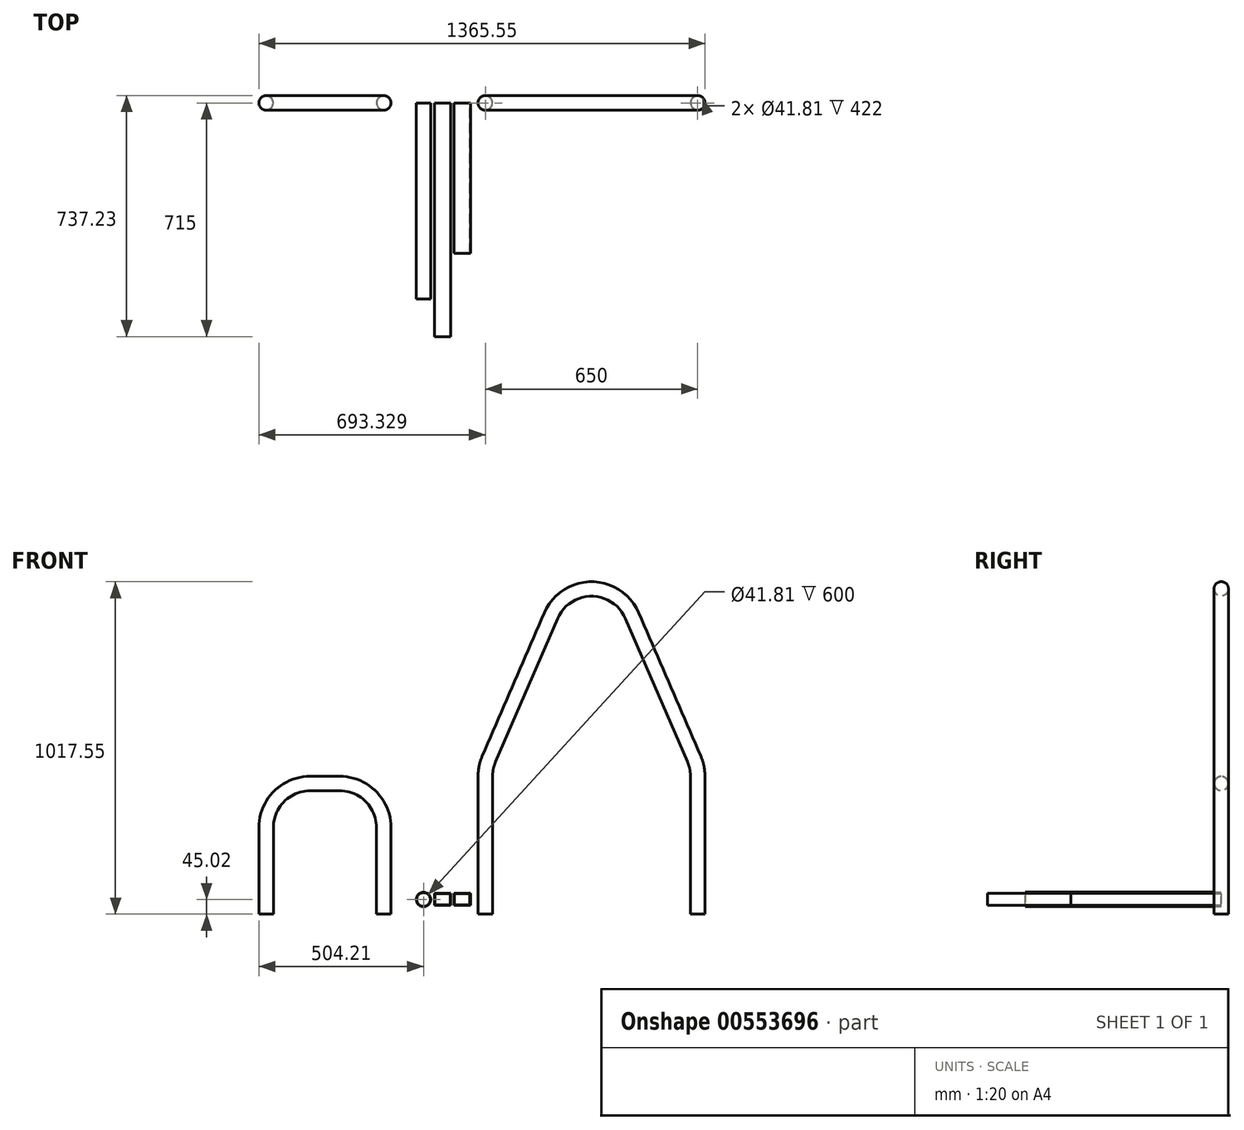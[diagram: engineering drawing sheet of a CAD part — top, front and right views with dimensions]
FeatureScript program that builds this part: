
annotation { "Feature Type Name" : "Feature", "Feature Type Description" : "" }
export const myFeature = defineFeature(function(context is Context, id is Id, definition is map)
    precondition{}
    {
        {
            var Q0;
            Q0=qCreatedBy(makeId("Front.planeOp"),FACE);
            var sketch = newSketch(context, id + "F0", { "sketchPlane" : qUnion([Q0])});
            skCircle(sketch, "E0", {"center": v(0, 0) * mm, "radius": 22.23 * mm});
            skCircle(sketch, "E1", {"center": v(0, 0) * mm, "radius": 20.9 * mm});
            skLineSegment(sketch, "E2.direction1", {"start": v(0, 0) * mm, "end": v(50, 0) * mm, "construction": true});
            skLineSegment(sketch, "E3.bottom", {"start": v(33.4, 18.7) * mm, "end": v(83.4, 18.7) * mm});
            skLineSegment(sketch, "E3.top", {"start": v(33.4, -18.35) * mm, "end": v(83.4, -18.35) * mm});
            skLineSegment(sketch, "E3.left", {"start": v(33.4, 18.7) * mm, "end": v(33.4, -18.35) * mm});
            skLineSegment(sketch, "E3.right", {"start": v(83.4, 18.7) * mm, "end": v(83.4, -18.35) * mm});
            skLineSegment(sketch, "E4.0", {"start": v(34.9, 17.2) * mm, "end": v(34.9, -16.85) * mm});
            skLineSegment(sketch, "E4.1", {"start": v(34.9, 17.2) * mm, "end": v(81.9, 17.2) * mm});
            skLineSegment(sketch, "E4.2", {"start": v(81.9, 17.2) * mm, "end": v(81.9, -16.85) * mm});
            skLineSegment(sketch, "E4.3", {"start": v(34.9, -16.85) * mm, "end": v(81.9, -16.85) * mm});
            skLineSegment(sketch, "E5.1.0.0", {"start": v(94.9, 17.2) * mm, "end": v(141.9, 17.2) * mm});
            skLineSegment(sketch, "E5.1.0.1", {"start": v(143.4, 18.7) * mm, "end": v(143.4, -18.35) * mm});
            skLineSegment(sketch, "E5.1.0.2", {"start": v(141.9, 17.2) * mm, "end": v(141.9, -16.85) * mm});
            skLineSegment(sketch, "E5.1.0.3", {"start": v(94.9, 17.2) * mm, "end": v(94.9, -16.85) * mm});
            skLineSegment(sketch, "E5.1.0.4", {"start": v(94.9, -16.85) * mm, "end": v(141.9, -16.85) * mm});
            skLineSegment(sketch, "E5.1.0.5", {"start": v(93.4, 18.7) * mm, "end": v(93.4, -18.35) * mm});
            skLineSegment(sketch, "E5.1.0.6", {"start": v(93.4, 18.7) * mm, "end": v(143.4, 18.7) * mm});
            skLineSegment(sketch, "E5.1.0.7", {"start": v(93.4, -18.35) * mm, "end": v(143.4, -18.35) * mm});
            skLineSegment(sketch, "E5.direction1", {"start": v(33.4, -18.35) * mm, "end": v(93.4, -18.35) * mm, "construction": true});
            skLineSegment(sketch, "E6.0", {"start": v(189.12, -45.02) * mm, "end": v(189.12, 376.98) * mm});
            skLineSegment(sketch, "E7", {"start": v(-121.99, -45.02) * mm, "end": v(-121.99, 219.98) * mm});
            skLineSegment(sketch, "E8.0", {"start": v(-481.99, -45.02) * mm, "end": v(-481.99, 219.98) * mm});
            skLineSegment(sketch, "E9", {"start": v(-346.99, 354.98) * mm, "end": v(-256.99, 354.98) * mm});
            skArc(sketch, "E10", {"start": v(-346.99, 354.98) * mm, "mid": v(-442.44, 315.44) * mm, "end": v(-481.99, 219.98) * mm});
            skArc(sketch, "E11", {"start": v(-121.99, 219.98) * mm, "mid": v(-161.53, 315.44) * mm, "end": v(-256.99, 354.98) * mm});
            skLineSegment(sketch, "E12.0", {"start": v(839.12, -45.02) * mm, "end": v(839.12, 376.98) * mm});
            skLineSegment(sketch, "E13.0", {"start": v(514.12, -52.24) * mm, "end": v(514.12, 1154.76) * mm});
            skPoint(sketch, "E14.visualSharp", {"position": v(514.12, 1154.76) * mm});
            skLineSegment(sketch, "E15", {"start": v(200.25, 430.67) * mm, "end": v(390.25, 869) * mm});
            skLineSegment(sketch, "E16", {"start": v(827.98, 430.67) * mm, "end": v(637.98, 869) * mm});
            skArc(sketch, "E17.filletArc", {"start": v(637.98, 869) * mm, "mid": v(514.12, 950.3) * mm, "end": v(390.25, 869) * mm});
            skPoint(sketch, "E18.visualSharp", {"position": v(189.12, 404.98) * mm});
            skArc(sketch, "E18.filletArc", {"start": v(200.25, 430.67) * mm, "mid": v(191.93, 404.4) * mm, "end": v(189.12, 376.98) * mm});
            skPoint(sketch, "E19.visualSharp", {"position": v(839.12, 404.98) * mm});
            skArc(sketch, "E19.filletArc", {"start": v(839.12, 376.98) * mm, "mid": v(836.3, 404.4) * mm, "end": v(827.98, 430.67) * mm});
            skLineSegment(sketch, "E20", {"start": v(-728.45, -45.02) * mm, "end": v(1281.65, -45.02) * mm, "construction": true});
            skLineSegment(sketch, "E21", {"start": v(168.51, 434.98) * mm, "end": v(927.4, 434.98) * mm, "construction": true});
            skSolve(sketch);
        }
        {
            var Q0;
            Q0=makeQuery(id+"F0.imprint","IMPRINT",FACE,{"disambiguationData":[TD([[makeQuery(id+"F0.imprint","IMPRINT",EDGE,{"derivedFrom":sQuery(id+"F0.wireOp",EDGE,"E0")}),1.0]])]});
            extrude(context, id + "F1", {"entities" : qUnion([Q0]), "depth" : 600 * mm, "offsetDistance" : 25 * mm});
        }
        {
            var Q0;
            Q0=makeQuery(id+"F0.imprint","IMPRINT",FACE,{"disambiguationData":[TD([[makeQuery(id+"F0.imprint","IMPRINT",EDGE,{"derivedFrom":sQuery(id+"F0.wireOp",EDGE,"E3.bottom")}),-1.0]])]});
            extrude(context, id + "F2", {"entities" : qUnion([Q0]), "depth" : 715 * mm, "offsetDistance" : 25 * mm});
        }
        {
            var Q0;
            Q0=makeQuery(id+"F0.imprint","IMPRINT",FACE,{"disambiguationData":[TD([[makeQuery(id+"F0.imprint","IMPRINT",EDGE,{"derivedFrom":sQuery(id+"F0.wireOp",EDGE,"E5.1.0.0")}),1.0]])]});
            extrude(context, id + "F3", {"entities" : qUnion([Q0]), "depth" : 460 * mm, "offsetDistance" : 25 * mm});
        }
        {
            var Q0;
            Q0=sQuery(id+"F0.wireOp",VERTEX,"E6.0.start");
            var Q1;
            Q1=makeQuery(id+"F3.opExtrude","SWEPT_FACE",FACE,{"disambiguationData":[OSD([sQuery(id+"F0.wireOp",EDGE,"E5.1.0.7")])]});
            cPlane(context, id + "F4", {"entities" : qUnion([Q0, Q1]), "cplaneType" : CPlaneType.PLANE_POINT, "offset" : 25 * mm, "width" : 150 * mm, "height" : 150 * mm});
        }
        {
            var Q0;
            Q0=qCreatedBy(id+"F4.planeOp",FACE);
            var sketch = newSketch(context, id + "F5", { "sketchPlane" : qUnion([Q0])});
            skCircle(sketch, "E22", {"center": v(189.12, 0) * mm, "radius": 22.23 * mm});
            skCircle(sketch, "E23", {"center": v(189.12, 0) * mm, "radius": 20.9 * mm});
            skCircle(sketch, "E24.1.0.0", {"center": v(-481.99, 0) * mm, "radius": 22.23 * mm});
            skCircle(sketch, "E24.1.0.1", {"center": v(-481.99, 0) * mm, "radius": 20.9 * mm});
            skSolve(sketch);
        }
        {
            var Q0;
            Q0=makeQuery(id+"F5.imprint","IMPRINT",FACE,{"disambiguationData":[TD([[makeQuery(id+"F5.imprint","IMPRINT",EDGE,{"derivedFrom":sQuery(id+"F5.wireOp",EDGE,"E22")}),1.0]])]});
            var Q1;
            Q1=sQuery(id+"F0.wireOp",EDGE,"E6.0");
            var Q2;
            Q2=sQuery(id+"F0.wireOp",EDGE,"E12.0");
            var Q3;
            Q3=sQuery(id+"F0.wireOp",EDGE,"E18.filletArc");
            var Q4;
            Q4=sQuery(id+"F0.wireOp",EDGE,"E15");
            var Q5;
            Q5=sQuery(id+"F0.wireOp",EDGE,"E17.filletArc");
            var Q6;
            Q6=sQuery(id+"F0.wireOp",EDGE,"E16");
            var Q7;
            Q7=sQuery(id+"F0.wireOp",EDGE,"E19.filletArc");
            sweep(context, id + "F6", {"profiles" : qUnion([Q0]), "path" : qUnion([Q1, Q2, Q3, Q4, Q5, Q6, Q7])});
        }
        {
            var Q0;
            Q0=makeQuery(id+"F5.imprint","IMPRINT",FACE,{"disambiguationData":[TD([[makeQuery(id+"F5.imprint","IMPRINT",EDGE,{"derivedFrom":sQuery(id+"F5.wireOp",EDGE,"E24.1.0.0")}),1.0]])]});
            var Q1;
            Q1=sQuery(id+"F0.wireOp",EDGE,"E8.0");
            var Q2;
            Q2=sQuery(id+"F0.wireOp",EDGE,"E10");
            var Q3;
            Q3=sQuery(id+"F0.wireOp",EDGE,"E9");
            var Q4;
            Q4=sQuery(id+"F0.wireOp",EDGE,"E11");
            var Q5;
            Q5=sQuery(id+"F0.wireOp",EDGE,"E7");
            sweep(context, id + "F7", {"profiles" : qUnion([Q0]), "path" : qUnion([Q1, Q2, Q3, Q4, Q5])});
        }
    });
